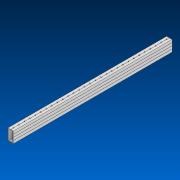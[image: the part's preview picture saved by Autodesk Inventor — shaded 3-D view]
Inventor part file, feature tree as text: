
AUTODESK INVENTOR PART (.ipt)
format: ipt  version: 2022.2 (Build 262287000, 287)  size: 514,560 bytes
history: native  units: in
note: dims shown in document units (in); Inventor stores cm internally (conversion verified against a paired STEP export)
features: other x30, extrude x1, pattern_linear x1, sketch x1
ambient origin geometry x8: Origin, YZ Plane, XZ Plane, XY Plane, X Axis, Y Axis, Z Axis, Center Point
bodies: Solid1 (feature_tree)
feature tree (33):
  extrude  "Extrusion1"  Depth=2.0in
  other  "Work Axis1"
  pattern_linear  "Rectangular Pattern1"  Spacing1=30.0in  [1 undecoded]
  sketch  "Sketch1"  dims[d0=1.0in d1=2.0in d2=30.0in d3=0.0in d4=11.4173in d6=1.0in]
  other  "Work Axis2"
  other  "Work Axis3"
  other  "Work Axis4"
  other  "Work Axis5"
  other  "Work Axis6"
  other  "Work Axis7"
  other  "Work Axis8"
  other  "Work Axis9"
  other  "Work Axis10"
  other  "Work Axis60"
  other  "Work Axis61"
  other  "Work Axis62"
  other  "Work Axis63"
  other  "Work Axis64"
  other  "Work Axis65"
  other  "Work Axis66"
  other  "Work Axis67"
  other  "Work Axis68"
  other  "Work Axis69"
  other  "Work Axis70"
  other  "Work Axis71"
  other  "Work Axis72"
  other  "Work Axis73"
  other  "Work Axis74"
  other  "Work Axis75"
  other  "Work Axis76"
  other  "Work Axis77"
  other  "Work Axis78"
  other  "Cut-Extrude2"
note: 1 required parameter value undecoded (feature->parameter linkage not recoverable at this tier; creation-order binding heuristic only, values carry confidence <= 0.55)
